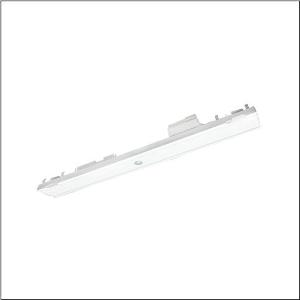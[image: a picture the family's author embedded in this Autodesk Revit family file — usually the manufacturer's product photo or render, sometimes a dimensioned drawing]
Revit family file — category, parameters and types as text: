
# Revit family: licross_r_56tl117c4x31_6d2f
name_source: partatom
category: Lighting Fixtures
units: mm (PartAtom-declared; Revit-internal decimal feet)

## family parameters
Cut with Voids When Loaded = No
Host = Face
Light Source = No
Part Type = Normal
Room Calculation Point = No
Round Connector Dimension = Use Diameter
Shared = No

## types (1)
- Licross® (1 x LED, 310 lm, 3.9 W, 4000K)
    Apparent Load = 4 VA
    CIE Flux Codes = 84 95 98 100 100
    Color Rendering = 70
    Color Temperature = 4000K
    Default Elevation = 1800 mm
    Description = Licross®, luminaire insert, of sheet steel, coil coated, white, length: 500mm, width: 59mm, height: 60mm, mounting height: 7..17m, emergency light element,LED rated luminous flux: 310lm, light colour: 740, control gear: CEAG, with plug, 6-pole, with phase selection, mains connection: 220..240V, AC/DC, 0/50..60Hz, rated input power: 3.9W, halogen-free wiring, for trunking rail, 9..14-pole, for emergency light function, supply monitoring module CEAG, with address switch, choice between two emergency light lines via tool-free moving of contact pin prior to installation in trunking rail, primary light control with lens, of PMMA, primary optical cover: cover, of PMMA, light emission: direct distribution, primary light characteristic: symmetric,  for area, compatible with all CEAG STAR technology systems (ZB-S, DG-S (DualGuard-S), LP-STAR, AT-S+), protection rating (complete): IP40, insulation class (complete): insulation class I (protective earthing), certification: CE, UKCA, protection symbol: D if used in an environment without relevant dust loads, impact resistance: IK06, permissible ambient temperature for indoor applications: -20..+40°C, packaging unit: 1 piece
    Height = 60 mm  [stored 0.19685 ft]
    Lamp = 1 x LED
    Lamp Light Flux = 310 lm
    Lamp Power = 3.9 W
    Lamp count = 1
    Length = 500 mm
    Luminous efficacy = 79 lm/W
    Manufacturer = Siteco
    ModVariant = No
    Model = 56TL117C4X31
    Mounting Place = Ceiling
    Mounting Type = Pendant
    Number of Poles = 1
    OnlyDefault = Yes
    Power Factor = 1
    Product Name = Licross®
    Product group = luminaire insert
    ProductGroupID = 901
    Protection Class = Protection class I
    Protection Degree = IP 40
    RLX_Detail_Level = 1
    RLX_Emergency_Light_Flux = 0 lm
    RLX_Emergency_Type = 0
    RLX_Emergency_Type_DB = No
    RlxData = <blob elided: 30933 chars, md5=bf09d66a>
    Socket = socket
    Standby Power = 0 W
    System Light Flux = 310 lm
    System Power = 4 W
    Type Comments = Product without accessories
    Type Image = l_1251804.jpg
    URL = http://relux.com
    VarID = ---
    Voltage = 0 V
    Weight = 0.00 kg
    Width = 59 mm

note: [stored X ft] marks values corroborated as IEEE doubles in the binary element streams (Revit-internal decimal feet)

## geometry (parser evidence)
native form markers: Blend x4, Sweep x10
no freeform markers — native parametric forms only
